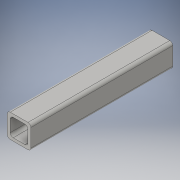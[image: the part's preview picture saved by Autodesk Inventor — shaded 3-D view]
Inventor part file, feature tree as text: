
AUTODESK INVENTOR PART (.ipt)
format: ipt  version: 2016 (Build 200138000, 138)  size: 112,640 bytes
history: native  units: in
note: dims shown in document units (in); Inventor stores cm internally (conversion verified against a paired STEP export)
features: extrude x1, sketch x1
ambient origin geometry x8: Origin, YZ Plane, XZ Plane, XY Plane, X Axis, Y Axis, Z Axis, Center Point
bodies: Solid1 (feature_tree)
feature tree (2):
  extrude  "Extrusion1"  Depth=1.0in
  sketch  "Sketch1"  dims[d0=1.0in d1=1.0in d2=0.125in d3=0.125in d4=6.0in d5=0.0in]
